# Revit family: Legacy_Water_Cooler-Non-filtered-Refrigerated-Elkay-EFA8L1Z
name_source: partatom
category: Plumbing Fixtures
units: mm (PartAtom-declared; Revit-internal decimal feet)

## family parameters
Always vertical = Yes
Cut with Voids When Loaded = No
Maintain Annotation Orientation = No
OmniClass Number = 23.45.05.14.14
OmniClass Title = Sinks/Lavatories
Part Type = Normal
Room Calculation Point = No
Round Connector Dimension = Use Diameter
Shared = No
Work Plane-Based = No

## types (1)
- EFA8L1Z (Legacy Floor Mount Cooler Non-filtered Refrigerated)
    Approx. Shipping Weight (lbs) = 72
    Assembly Code = D2010800
    CW Connection = No
    Chilling Capacity = 8.0 GPH
    Default Elevation = 0 "
    Description = Legacy Floor Mount Cooler Non-filtered Refrigerated 8 GPH Light Gray Granite
    Dimensions (L x W x H) = 18 inch x 14 1/2 inch x 41 1/2 inch
    Frnt pnl Len. = 10.85 "
    Inlet Connection Size (inch) = 0.375 "
    Installation Location = Indoor
    Main Material = Finish-Elkay-Light Gray Granite
    Manufacturer = Elkay (by Zurn Elkay Water Solutions)
    Manufacturer Brand = Elkay Manufacturer Company
    Model = EFA8L1Z
    Mounting Type = Floor Mount/Freestanding
    Outlet Connection Size (inch) = 1.25 "
    Product Documentation Link = https://www.elkayfiles.com
    Product Installation Sheet URL = https://www.elkayfiles.com
    Product Page URL = https://www.elkay.com
    Product Weight (lbs) = 60
    Product data URL = https://www.bimobject.com
    Repair Parts URL = https://www.elkayfiles.com
    Sink Height = 41.5 "
    Sink Length = 18 "
    Sink Width = 14.5 "
    URL = https://www.elkay.com
    Waste Connection = No

## geometry (parser evidence)
native form markers: Sweep x6
no freeform markers — native parametric forms only
